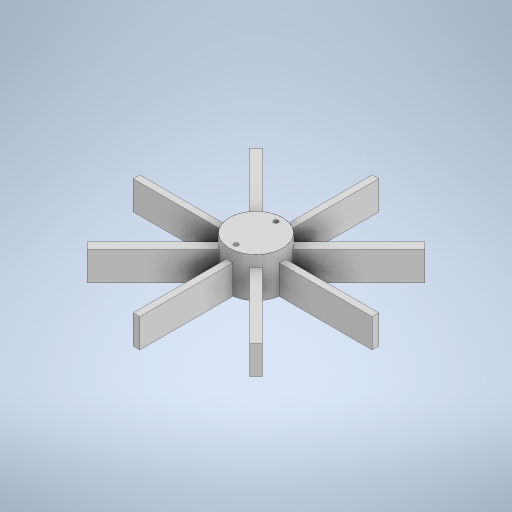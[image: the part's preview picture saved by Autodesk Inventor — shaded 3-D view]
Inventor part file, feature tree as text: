
AUTODESK INVENTOR PART (.ipt)
format: ipt  version: 2024 (Build 280153000, 153)  size: 300,032 bytes
history: native  units: in
note: dims shown in document units (in); Inventor stores cm internally (conversion verified against a paired STEP export)
features: extrude x3, sketch x3
ambient origin geometry x8: Origin, YZ Plane, XZ Plane, XY Plane, X Axis, Y Axis, Z Axis, Center Point
bodies: Solid1 (feature_tree)
feature tree (6):
  extrude  "Extrusion1"  Depth=4.252in
  extrude  "Extrusion2"  Depth=4.252in
  extrude  "Extrusion3"  Depth=0.1181in
  sketch  "Sketch2"  dims[d0=0.9449in d1=4.252in]
  sketch  "Sketch3"  dims[d2=0.1181in d3=4.252in]
  sketch  "Sketch4"  dims[d4=0.1181in d5=2.126in d6=2.126in d7=2.126in d8=2.126in d9=0.5118in d10=0.0in d11=0.9449in d12=0.1969in d13=0.0in d14=0.1181in d15=0.1181in d16=0.0787in d17=0.0787in d18=0.7874in d19=0.0in d20=0.0197in d21=0.0344in]
